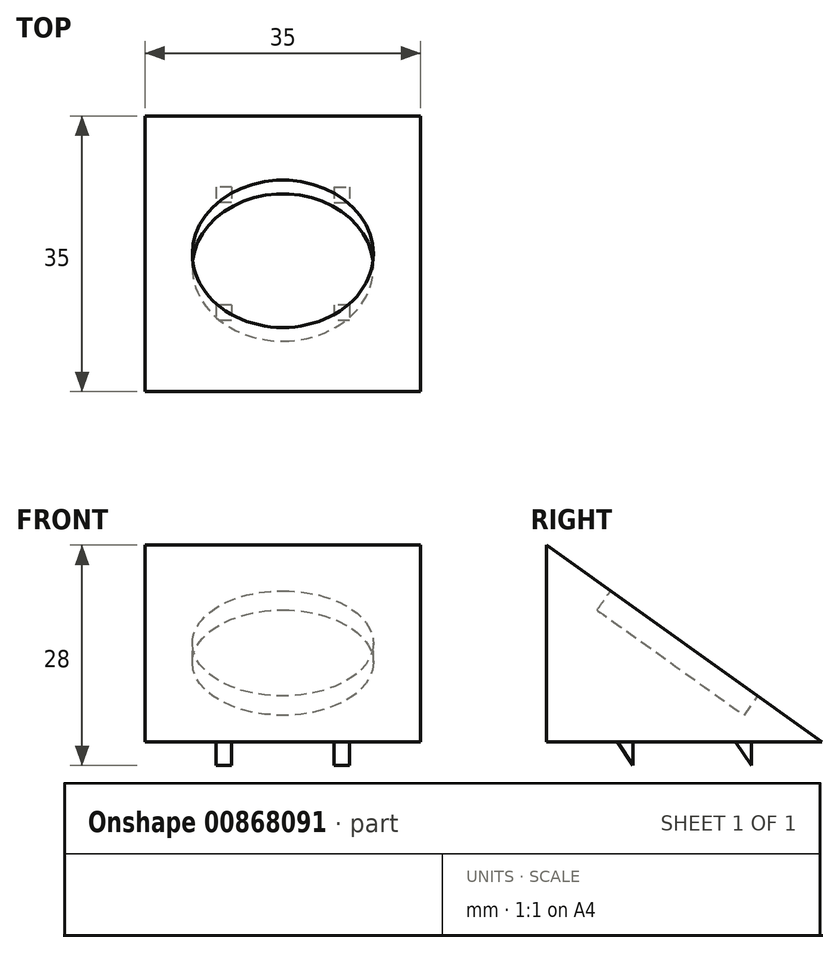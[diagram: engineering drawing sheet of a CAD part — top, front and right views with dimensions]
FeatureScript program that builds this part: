
annotation { "Feature Type Name" : "Feature", "Feature Type Description" : "" }
export const myFeature = defineFeature(function(context is Context, id is Id, definition is map)
    precondition{}
    {
        {
            var Q0;
            Q0=qCreatedBy(makeId("Top.planeOp"),FACE);
            var sketch = newSketch(context, id + "F0", { "sketchPlane" : qUnion([Q0])});
            skLineSegment(sketch, "E0.bottom", {"start": v(17.5, 17.5) * mm, "end": v(-17.5, 17.5) * mm});
            skLineSegment(sketch, "E0.top", {"start": v(17.5, -17.5) * mm, "end": v(-17.5, -17.5) * mm});
            skLineSegment(sketch, "E0.left", {"start": v(17.5, 17.5) * mm, "end": v(17.5, -17.5) * mm});
            skLineSegment(sketch, "E0.right", {"start": v(-17.5, 17.5) * mm, "end": v(-17.5, -17.5) * mm});
            skPoint(sketch, "E0.middle", {"position": v(0, 0) * mm});
            skLineSegment(sketch, "E1", {"start": v(-7.5, 17.5) * mm, "end": v(-7.5, -17.5) * mm, "construction": true});
            skLineSegment(sketch, "E2", {"start": v(7.5, 17.5) * mm, "end": v(7.5, -17.5) * mm, "construction": true});
            skLineSegment(sketch, "E3", {"start": v(-17.5, 17.5) * mm, "end": v(17.5, -17.5) * mm, "construction": true});
            skLineSegment(sketch, "E4", {"start": v(17.5, 17.5) * mm, "end": v(-17.5, -17.5) * mm, "construction": true});
            skLineSegment(sketch, "E5.bottom", {"start": v(-6.5, 8.5) * mm, "end": v(-8.5, 8.5) * mm});
            skLineSegment(sketch, "E5.top", {"start": v(-6.5, 6.5) * mm, "end": v(-8.5, 6.5) * mm});
            skLineSegment(sketch, "E5.left", {"start": v(-6.5, 8.5) * mm, "end": v(-6.5, 6.5) * mm});
            skLineSegment(sketch, "E5.right", {"start": v(-8.5, 8.5) * mm, "end": v(-8.5, 6.5) * mm});
            skPoint(sketch, "E5.middle", {"position": v(-7.5, 7.5) * mm});
            skLineSegment(sketch, "E6.bottom", {"start": v(6.5, 8.5) * mm, "end": v(8.5, 8.5) * mm});
            skLineSegment(sketch, "E6.top", {"start": v(6.5, 6.5) * mm, "end": v(8.5, 6.5) * mm});
            skLineSegment(sketch, "E6.left", {"start": v(6.5, 8.5) * mm, "end": v(6.5, 6.5) * mm});
            skLineSegment(sketch, "E6.right", {"start": v(8.5, 8.5) * mm, "end": v(8.5, 6.5) * mm});
            skPoint(sketch, "E6.middle", {"position": v(7.5, 7.5) * mm});
            skLineSegment(sketch, "E7.bottom", {"start": v(8.5, -6.5) * mm, "end": v(6.5, -6.5) * mm});
            skLineSegment(sketch, "E7.top", {"start": v(8.5, -8.5) * mm, "end": v(6.5, -8.5) * mm});
            skLineSegment(sketch, "E7.left", {"start": v(8.5, -6.5) * mm, "end": v(8.5, -8.5) * mm});
            skLineSegment(sketch, "E7.right", {"start": v(6.5, -6.5) * mm, "end": v(6.5, -8.5) * mm});
            skPoint(sketch, "E7.middle", {"position": v(7.5, -7.5) * mm});
            skLineSegment(sketch, "E8.bottom", {"start": v(-6.5, -6.5) * mm, "end": v(-8.5, -6.5) * mm});
            skLineSegment(sketch, "E8.top", {"start": v(-6.5, -8.5) * mm, "end": v(-8.5, -8.5) * mm});
            skLineSegment(sketch, "E8.left", {"start": v(-6.5, -6.5) * mm, "end": v(-6.5, -8.5) * mm});
            skLineSegment(sketch, "E8.right", {"start": v(-8.5, -6.5) * mm, "end": v(-8.5, -8.5) * mm});
            skPoint(sketch, "E8.middle", {"position": v(-7.5, -7.5) * mm});
            skSolve(sketch);
        }
        {
            var Q0;
            Q0=makeQuery(id+"F0.imprint","IMPRINT",FACE,{"disambiguationData":[TD([[makeQuery(id+"F0.imprint","IMPRINT",EDGE,{"derivedFrom":sQuery(id+"F0.wireOp",EDGE,"E0.bottom")}),1.0]])]});
            var Q1;
            Q1=makeQuery(id+"F0.imprint","IMPRINT",FACE,{"disambiguationData":[TD([[makeQuery(id+"F0.imprint","IMPRINT",EDGE,{"derivedFrom":sQuery(id+"F0.wireOp",EDGE,"E6.bottom")}),-1.0]])]});
            var Q2;
            Q2=makeQuery(id+"F0.imprint","IMPRINT",FACE,{"disambiguationData":[TD([[makeQuery(id+"F0.imprint","IMPRINT",EDGE,{"derivedFrom":sQuery(id+"F0.wireOp",EDGE,"E5.bottom")}),1.0]])]});
            var Q3;
            Q3=makeQuery(id+"F0.imprint","IMPRINT",FACE,{"disambiguationData":[TD([[makeQuery(id+"F0.imprint","IMPRINT",EDGE,{"derivedFrom":sQuery(id+"F0.wireOp",EDGE,"E8.bottom")}),1.0]])]});
            var Q4;
            Q4=makeQuery(id+"F0.imprint","IMPRINT",FACE,{"disambiguationData":[TD([[makeQuery(id+"F0.imprint","IMPRINT",EDGE,{"derivedFrom":sQuery(id+"F0.wireOp",EDGE,"E7.bottom")}),1.0]])]});
            extrude(context, id + "F1", {"entities" : qUnion([Q0, Q1, Q2, Q3, Q4]), "depth" : 25 * mm, "offsetDistance" : 25 * mm});
        }
        {
            var Q0;
            Q0=makeQuery(id+"F1.opExtrude","CAP_EDGE",EDGE,{"disambiguationData":[OSD([sQuery(id+"F0.wireOp",EDGE,"E0.bottom")])],"isStart":false});
            chamfer(context, id + "F2", {"entities" : qUnion([Q0]), "chamferType" : ChamferType.TWO_OFFSETS, "width1" : 35 * mm, "oppositeDirection" : false, "width2" : 25 * mm, "tangentPropagation" : true});
        }
        {
            var Q0;
            Q0=makeQuery(id+"F0.imprint","IMPRINT",FACE,{"disambiguationData":[TD([[makeQuery(id+"F0.imprint","IMPRINT",EDGE,{"derivedFrom":sQuery(id+"F0.wireOp",EDGE,"E6.bottom")}),-1.0]])]});
            var Q1;
            Q1=makeQuery(id+"F0.imprint","IMPRINT",FACE,{"disambiguationData":[TD([[makeQuery(id+"F0.imprint","IMPRINT",EDGE,{"derivedFrom":sQuery(id+"F0.wireOp",EDGE,"E5.bottom")}),1.0]])]});
            var Q2;
            Q2=makeQuery(id+"F0.imprint","IMPRINT",FACE,{"disambiguationData":[TD([[makeQuery(id+"F0.imprint","IMPRINT",EDGE,{"derivedFrom":sQuery(id+"F0.wireOp",EDGE,"E8.bottom")}),1.0]])]});
            var Q3;
            Q3=makeQuery(id+"F0.imprint","IMPRINT",FACE,{"disambiguationData":[TD([[makeQuery(id+"F0.imprint","IMPRINT",EDGE,{"derivedFrom":sQuery(id+"F0.wireOp",EDGE,"E7.bottom")}),1.0]])]});
            extrude(context, id + "F3", {"entities" : qUnion([Q0, Q1, Q2, Q3]), "operationType" : NewBodyOperationType.ADD, "oppositeDirection" : true, "depth" : 3 * mm, "offsetDistance" : 25 * mm});
        }
        {
            var Q0;
            Q0=makeQuery(id+"F2.opChamfer","BLEND_FACE",FACE,{"disambiguationData":[OSD([sQuery(id+"F0.wireOp",EDGE,"E0.bottom")])]});
            var sketch = newSketch(context, id + "F4", { "sketchPlane" : qUnion([Q0])});
            skLineSegment(sketch, "E9", {"start": v(-17.5, 14.24) * mm, "end": v(17.5, -28.77) * mm, "construction": true});
            skLineSegment(sketch, "E10", {"start": v(17.5, -28.77) * mm, "end": v(-17.5, -28.77) * mm, "construction": true});
            skLineSegment(sketch, "E11", {"start": v(-17.5, -28.77) * mm, "end": v(17.5, 14.24) * mm, "construction": true});
            skCircle(sketch, "E12", {"center": v(0, -7.27) * mm, "radius": 11.5 * mm});
            skSolve(sketch);
        }
        {
            var Q0;
            Q0 = qSketchRegion(id + "F4", true);
            extrude(context, id + "F5", {"entities" : qUnion([Q0]), "operationType" : NewBodyOperationType.REMOVE, "oppositeDirection" : true, "depth" : 3 * mm, "offsetDistance" : 25 * mm});
        }
        {
            var Q0;
            Q0=makeQuery(id+"F3.opExtrude","CAP_EDGE",EDGE,{"disambiguationData":[OSD([sQuery(id+"F0.wireOp",EDGE,"E6.top")])],"isStart":false});
            chamfer(context, id + "F6", {"entities" : qUnion([Q0]), "chamferType" : ChamferType.TWO_OFFSETS, "width1" : 3 * mm, "oppositeDirection" : false, "width2" : 2 * mm, "tangentPropagation" : true});
        }
        {
            var Q0;
            Q0=makeQuery(id+"F3.opExtrude","CAP_EDGE",EDGE,{"disambiguationData":[OSD([sQuery(id+"F0.wireOp",EDGE,"E5.top")])],"isStart":false});
            var Q1;
            Q1=makeQuery(id+"F3.opExtrude","CAP_EDGE",EDGE,{"disambiguationData":[OSD([sQuery(id+"F0.wireOp",EDGE,"E7.top")])],"isStart":false});
            var Q2;
            Q2=makeQuery(id+"F3.opExtrude","CAP_EDGE",EDGE,{"disambiguationData":[OSD([sQuery(id+"F0.wireOp",EDGE,"E8.top")])],"isStart":false});
            chamfer(context, id + "F7", {"entities" : qUnion([Q0, Q1, Q2]), "chamferType" : ChamferType.TWO_OFFSETS, "width1" : 2 * mm, "oppositeDirection" : false, "width2" : 3 * mm, "tangentPropagation" : true});
        }
    });
